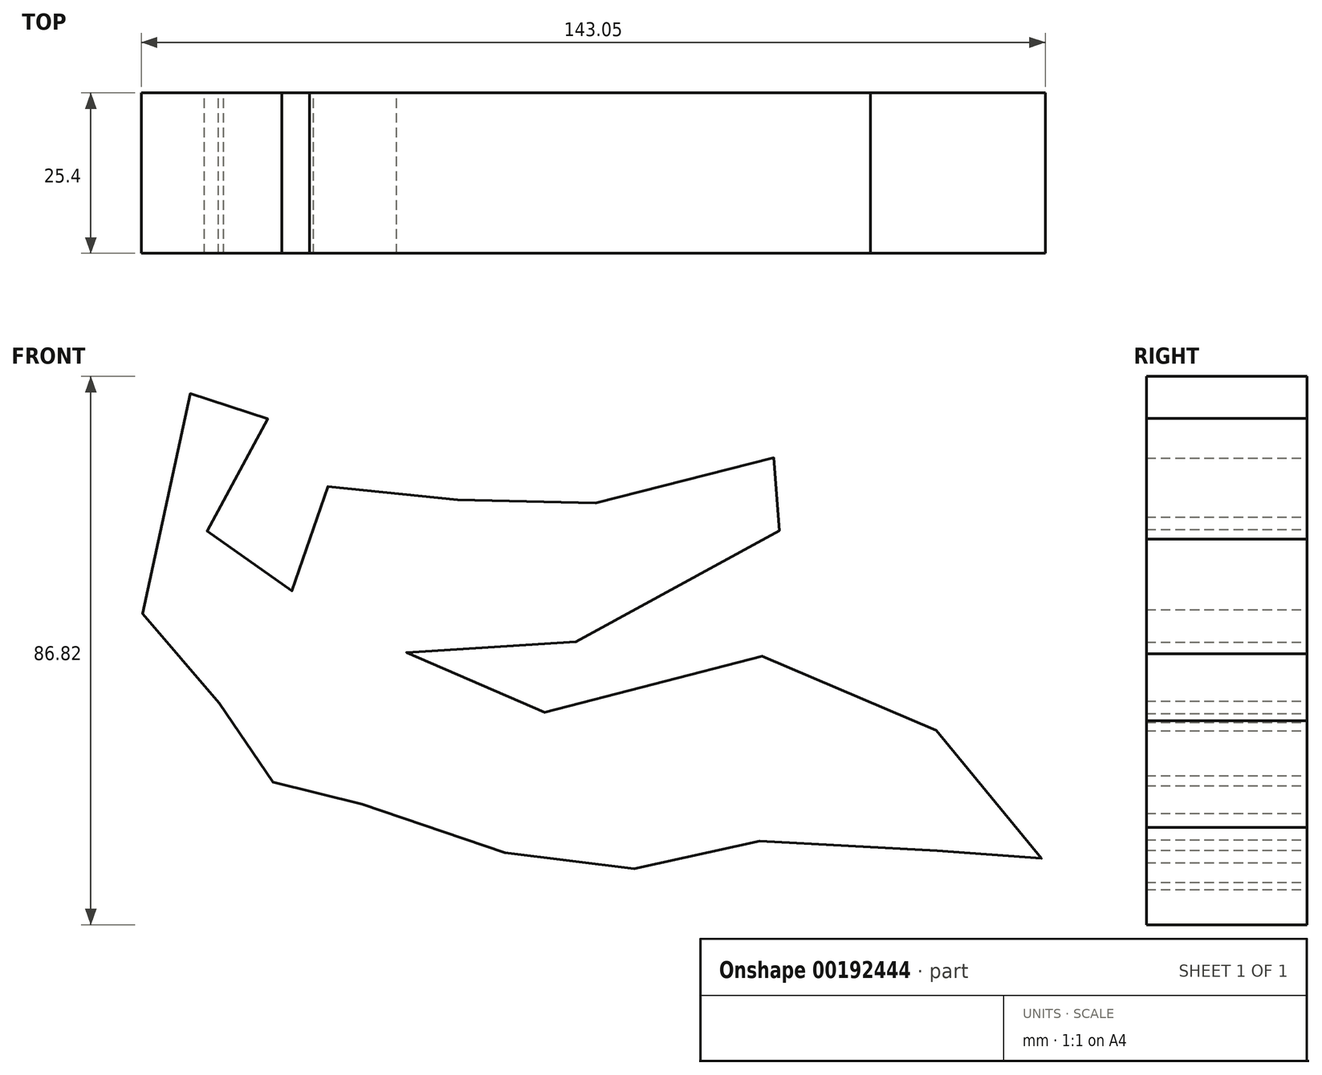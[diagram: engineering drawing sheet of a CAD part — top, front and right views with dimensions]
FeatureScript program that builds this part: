
annotation { "Feature Type Name" : "Feature", "Feature Type Description" : "" }
export const myFeature = defineFeature(function(context is Context, id is Id, definition is map)
    precondition{}
    {
        {
            var Q0;
            Q0=qCreatedBy(makeId("Front.planeOp"),FACE);
            var sketch = newSketch(context, id + "F0", { "sketchPlane" : qUnion([Q0])});
            skFitSpline(sketch, "E0", {"points": [v(-67.67, -14.78) * mm, v(-67.06, -32.16) * mm, v(-56.08, -26.37) * mm, v(-51.51, -36.42) * mm, v(-39.93, -27.89) * mm, v(-25, -40.08) * mm, v(-13.41, -27.89) * mm, v(2.13, -44.35) * mm, v(12.8, -34.6) * mm, v(27.74, -43.13) * mm, v(47.24, -38.56) * mm, v(58.52, -49.83) * mm, v(60.66, -19.66) * mm, v(41.76, -19.05) * mm, v(22.25, -7.16) * mm, v(3.35, -14.48) * mm, v(-25.9, -14.48) * mm, v(-32, -10.52) * mm, v(-39.62, -5.33) * mm, v(-13.41, -5.94) * mm, v(10.67, 12.04) * mm, v(35.36, 12.04) * mm, v(0, 30.02) * mm, v(-8.53, 16) * mm, v(-13.1, 14.78) * mm, v(-29.57, 17.22) * mm, v(-40.23, 23.93) * mm, v(-50.9, 19.05) * mm, v(-53.34, 12.65) * mm, v(-53.04, 7.16) * mm, v(-62.48, 0) * mm, v(-69.8, 6.25) * mm, v(-67.97, 19.35) * mm, v(-65.84, 26.06) * mm, v(-57.91, 32.46) * mm, v(-60.66, 36.42) * mm, v(-72.54, 33.99) * mm, v(-78.33, 15.4) * mm, v(-76.8, -17.83) * mm, v(-67.67, -14.78) * mm]});
            skSolve(sketch);
        }
        {
            var Q0;
            Q0 = qSketchRegion(id + "F0", true);
            var Q1;
            Q1=makeQuery(id+"F0.imprint","IMPRINT",FACE,{"disambiguationData":[TD([[makeQuery(id+"F0.imprint","IMPRINT",EDGE,{"derivedFrom":sQuery(id+"F0.wireOp",EDGE,"E0")}),1.0]])]});
            extrude(context, id + "F1", {"entities" : qUnion([Q0, Q1]), "depth" : 25.4 * mm});
        }
    });
